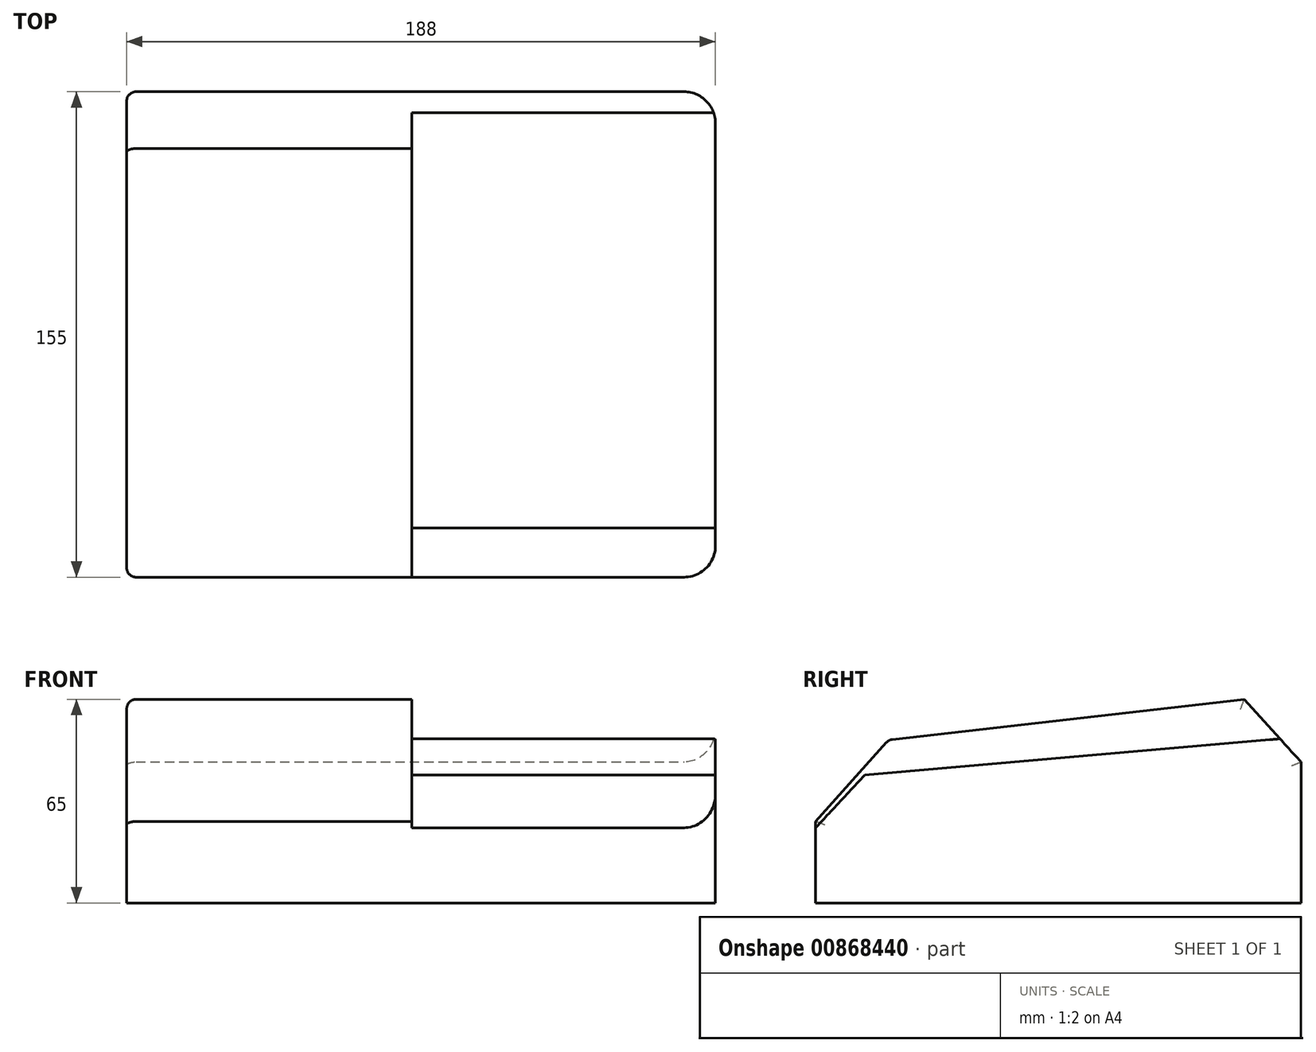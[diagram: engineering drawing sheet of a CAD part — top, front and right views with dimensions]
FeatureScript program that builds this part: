
annotation { "Feature Type Name" : "Feature", "Feature Type Description" : "" }
export const myFeature = defineFeature(function(context is Context, id is Id, definition is map)
    precondition{}
    {
        {
            var Q0;
            Q0=qCreatedBy(makeId("Top.planeOp"),FACE);
            var sketch = newSketch(context, id + "F0", { "sketchPlane" : qUnion([Q0])});
            skLineSegment(sketch, "E0.bottom", {"start": v(0, 155) * mm, "end": v(188, 155) * mm});
            skLineSegment(sketch, "E0.top", {"start": v(0, 0) * mm, "end": v(188, 0) * mm});
            skLineSegment(sketch, "E0.left", {"start": v(0, 155) * mm, "end": v(0, 0) * mm});
            skLineSegment(sketch, "E0.right", {"start": v(188, 155) * mm, "end": v(188, 0) * mm});
            skPoint(sketch, "E1", {"position": v(0, 77.5) * mm});
            skCircle(sketch, "E2", {"center": v(15, 141) * mm, "radius": 4 * mm});
            skCircle(sketch, "E3", {"center": v(175, 141) * mm, "radius": 4 * mm});
            skCircle(sketch, "E4", {"center": v(175, 15) * mm, "radius": 4 * mm});
            skCircle(sketch, "E5", {"center": v(15, 15) * mm, "radius": 4 * mm});
            skLineSegment(sketch, "E6", {"start": v(0, 150) * mm, "end": v(15, 150) * mm});
            skLineSegment(sketch, "E7", {"start": v(15, 132) * mm, "end": v(0, 132) * mm});
            skArc(sketch, "E8", {"start": v(15, 150) * mm, "mid": v(6, 141) * mm, "end": v(15, 132) * mm, "construction": true});
            skArc(sketch, "E9", {"start": v(15, 132) * mm, "mid": v(24, 141) * mm, "end": v(15, 150) * mm});
            skLineSegment(sketch, "E10", {"start": v(15, 24) * mm, "end": v(0, 24) * mm});
            skLineSegment(sketch, "E11", {"start": v(15, 6) * mm, "end": v(0, 6) * mm});
            skLineSegment(sketch, "E12", {"start": v(175, 24) * mm, "end": v(188, 24) * mm});
            skLineSegment(sketch, "E13", {"start": v(175, 6) * mm, "end": v(188, 6) * mm});
            skLineSegment(sketch, "E14", {"start": v(175, 150) * mm, "end": v(188, 150) * mm});
            skLineSegment(sketch, "E15", {"start": v(175, 132) * mm, "end": v(188, 132) * mm});
            skArc(sketch, "E16", {"start": v(175, 150) * mm, "mid": v(166, 141) * mm, "end": v(175, 132) * mm});
            skArc(sketch, "E17", {"start": v(175, 132) * mm, "mid": v(184, 141) * mm, "end": v(175, 150) * mm, "construction": true});
            skArc(sketch, "E18", {"start": v(175, 24) * mm, "mid": v(166, 15) * mm, "end": v(175, 6) * mm});
            skArc(sketch, "E19", {"start": v(175, 6) * mm, "mid": v(184, 15) * mm, "end": v(175, 24) * mm, "construction": true});
            skArc(sketch, "E20", {"start": v(15, 6) * mm, "mid": v(24, 15) * mm, "end": v(15, 24) * mm});
            skArc(sketch, "E21", {"start": v(15, 24) * mm, "mid": v(6, 15) * mm, "end": v(15, 6) * mm, "construction": true});
            skLineSegment(sketch, "E22.0", {"start": v(3, 3) * mm, "end": v(185, 3) * mm});
            skLineSegment(sketch, "E22.1", {"start": v(3, 152) * mm, "end": v(3, 3) * mm});
            skLineSegment(sketch, "E22.2", {"start": v(3, 152) * mm, "end": v(185, 152) * mm});
            skLineSegment(sketch, "E22.3", {"start": v(185, 152) * mm, "end": v(185, 3) * mm});
            skSolve(sketch);
        }
        {
            var Q0;
            {var subQ11=sQuery(id+"F0.wireOp",EDGE,"E9");Q0=makeQuery(id+"F0.imprint","IMPRINT",FACE,{"disambiguationData":[TD([[makeQuery(id+"F0.imprint","IMPRINT",EDGE,{"derivedFrom":subQ11}),-1.0]])]});}
            var Q1;
            {var subQ6=sQuery(id+"F0.wireOp",EDGE,"E0.bottom");Q1=makeQuery(id+"F0.imprint","IMPRINT",FACE,{"disambiguationData":[TD([[makeQuery(id+"F0.imprint","IMPRINT",EDGE,{"derivedFrom":subQ6}),-1.0]])]});}
            var Q2;
            Q2=makeQuery(id+"F0.imprint","IMPRINT",FACE,{"disambiguationData":[TD([[makeQuery(id+"F0.imprint","IMPRINT",EDGE,{"derivedFrom":sQuery(id+"F0.wireOp",EDGE,"E2")}),-1.0]])]});
            var Q3;
            {var subQ0=sQuery(id+"F0.wireOp",EDGE,"E6");var subQ1=sQuery(id+"F0.wireOp",EDGE,"E0.left");var subQ2=makeQuery(id+"F0.imprint","INTERSECT",VERTEX,{"derivedFrom":[subQ1,subQ0]});Q3=makeQuery(id+"F0.imprint","IMPRINT",FACE,{"disambiguationData":[TD([[makeQuery(id+"F0.imprint","IMPRINT",EDGE,{"disambiguationData":[TD([[subQ2,-1.0]])],"derivedFrom":subQ1}),1.0]])]});}
            var Q4;
            Q4=makeQuery(id+"F0.imprint","IMPRINT",FACE,{"disambiguationData":[TD([[makeQuery(id+"F0.imprint","IMPRINT",EDGE,{"derivedFrom":sQuery(id+"F0.wireOp",EDGE,"E2")}),1.0]])]});
            var Q5;
            {var subQ0=sQuery(id+"F0.wireOp",EDGE,"E7");var subQ1=sQuery(id+"F0.wireOp",EDGE,"E0.left");var subQ2=makeQuery(id+"F0.imprint","INTERSECT",VERTEX,{"derivedFrom":[subQ1,subQ0]});Q5=makeQuery(id+"F0.imprint","IMPRINT",FACE,{"disambiguationData":[TD([[makeQuery(id+"F0.imprint","IMPRINT",EDGE,{"disambiguationData":[TD([[subQ2,-1.0]])],"derivedFrom":subQ1}),1.0]])]});}
            var Q6;
            Q6=makeQuery(id+"F0.imprint","IMPRINT",FACE,{"disambiguationData":[TD([[makeQuery(id+"F0.imprint","IMPRINT",EDGE,{"derivedFrom":sQuery(id+"F0.wireOp",EDGE,"E5")}),-1.0]])]});
            var Q7;
            Q7=makeQuery(id+"F0.imprint","IMPRINT",FACE,{"disambiguationData":[TD([[makeQuery(id+"F0.imprint","IMPRINT",EDGE,{"derivedFrom":sQuery(id+"F0.wireOp",EDGE,"E5")}),1.0]])]});
            var Q8;
            {var subQ0=sQuery(id+"F0.wireOp",EDGE,"E10");var subQ1=sQuery(id+"F0.wireOp",EDGE,"E0.left");var subQ2=makeQuery(id+"F0.imprint","INTERSECT",VERTEX,{"derivedFrom":[subQ1,subQ0]});Q8=makeQuery(id+"F0.imprint","IMPRINT",FACE,{"disambiguationData":[TD([[makeQuery(id+"F0.imprint","IMPRINT",EDGE,{"disambiguationData":[TD([[subQ2,-1.0]])],"derivedFrom":subQ1}),1.0]])]});}
            var Q9;
            {var subQ6=sQuery(id+"F0.wireOp",EDGE,"E0.top");Q9=makeQuery(id+"F0.imprint","IMPRINT",FACE,{"disambiguationData":[TD([[makeQuery(id+"F0.imprint","IMPRINT",EDGE,{"derivedFrom":subQ6}),1.0]])]});}
            var Q10;
            Q10=makeQuery(id+"F0.imprint","IMPRINT",FACE,{"disambiguationData":[TD([[makeQuery(id+"F0.imprint","IMPRINT",EDGE,{"derivedFrom":sQuery(id+"F0.wireOp",EDGE,"E4")}),-1.0]])]});
            var Q11;
            Q11=makeQuery(id+"F0.imprint","IMPRINT",FACE,{"disambiguationData":[TD([[makeQuery(id+"F0.imprint","IMPRINT",EDGE,{"derivedFrom":sQuery(id+"F0.wireOp",EDGE,"E4")}),1.0]])]});
            var Q12;
            {var subQ0=sQuery(id+"F0.wireOp",EDGE,"E12");var subQ1=sQuery(id+"F0.wireOp",EDGE,"E0.right");var subQ2=makeQuery(id+"F0.imprint","INTERSECT",VERTEX,{"derivedFrom":[subQ1,subQ0]});Q12=makeQuery(id+"F0.imprint","IMPRINT",FACE,{"disambiguationData":[TD([[makeQuery(id+"F0.imprint","IMPRINT",EDGE,{"disambiguationData":[TD([[subQ2,-1.0]])],"derivedFrom":subQ1}),-1.0]])]});}
            var Q13;
            {var subQ0=sQuery(id+"F0.wireOp",EDGE,"E12");var subQ1=sQuery(id+"F0.wireOp",EDGE,"E0.right");var subQ2=makeQuery(id+"F0.imprint","INTERSECT",VERTEX,{"derivedFrom":[subQ1,subQ0]});Q13=makeQuery(id+"F0.imprint","IMPRINT",FACE,{"disambiguationData":[TD([[makeQuery(id+"F0.imprint","IMPRINT",EDGE,{"disambiguationData":[TD([[subQ2,1.0]])],"derivedFrom":subQ1}),-1.0]])]});}
            var Q14;
            {var subQ0=sQuery(id+"F0.wireOp",EDGE,"E14");var subQ1=sQuery(id+"F0.wireOp",EDGE,"E0.right");var subQ2=makeQuery(id+"F0.imprint","INTERSECT",VERTEX,{"derivedFrom":[subQ1,subQ0]});Q14=makeQuery(id+"F0.imprint","IMPRINT",FACE,{"disambiguationData":[TD([[makeQuery(id+"F0.imprint","IMPRINT",EDGE,{"disambiguationData":[TD([[subQ2,-1.0]])],"derivedFrom":subQ1}),-1.0]])]});}
            var Q15;
            Q15=makeQuery(id+"F0.imprint","IMPRINT",FACE,{"disambiguationData":[TD([[makeQuery(id+"F0.imprint","IMPRINT",EDGE,{"derivedFrom":sQuery(id+"F0.wireOp",EDGE,"E3")}),-1.0]])]});
            var Q16;
            Q16=makeQuery(id+"F0.imprint","IMPRINT",FACE,{"disambiguationData":[TD([[makeQuery(id+"F0.imprint","IMPRINT",EDGE,{"derivedFrom":sQuery(id+"F0.wireOp",EDGE,"E3")}),1.0]])]});
            extrude(context, id + "F1", {"entities" : qUnion([Q0, Q1, Q2, Q3, Q4, Q5, Q6, Q7, Q8, Q9, Q10, Q11, Q12, Q13, Q14, Q15, Q16]), "depth" : 65 * mm, "offsetDistance" : 25 * mm});
        }
        {
            var Q0;
            Q0=makeQuery(id+"F1.opExtrude","SWEPT_FACE",FACE,{"disambiguationData":[OSD([sQuery(id+"F0.wireOp",EDGE,"E0.right")])]});
            var sketch = newSketch(context, id + "F2", { "sketchPlane" : qUnion([Q0])});
            skLineSegment(sketch, "E23.0.0", {"start": v(0, 0) * mm, "end": v(155, 0) * mm});
            skLineSegment(sketch, "E23.0.1", {"start": v(155, 0) * mm, "end": v(155, 65) * mm});
            skLineSegment(sketch, "E23.0.2", {"start": v(155, 65) * mm, "end": v(0, 65) * mm});
            skLineSegment(sketch, "E23.0.3", {"start": v(0, 65) * mm, "end": v(0, 0) * mm});
            skLineSegment(sketch, "E24", {"start": v(0, 24) * mm, "end": v(15.69, 40.82) * mm});
            skLineSegment(sketch, "E25", {"start": v(15.69, 40.82) * mm, "end": v(148.28, 52.4) * mm});
            skLineSegment(sketch, "E26", {"start": v(155, 45) * mm, "end": v(136.86, 65) * mm});
            skLineSegment(sketch, "E27", {"start": v(136.86, 65) * mm, "end": v(23.36, 52.06) * mm});
            skLineSegment(sketch, "E28", {"start": v(23.36, 52.06) * mm, "end": v(0, 26) * mm});
            skSolve(sketch);
        }
        {
            var Q0;
            {var subQ3=sQuery(id+"F2.wireOp",EDGE,"E27");Q0=makeQuery(id+"F2.imprint","IMPRINT",FACE,{"disambiguationData":[TD([[makeQuery(id+"F2.imprint","IMPRINT",EDGE,{"derivedFrom":subQ3}),-1.0]])]});}
            var Q1;
            {var subQ0=sQuery(id+"F2.wireOp",EDGE,"E23.0.2");var subQ1=sQuery(id+"F2.wireOp",EDGE,"E23.0.1");var subQ2=makeQuery(id+"F2.imprint","INTERSECT",VERTEX,{"derivedFrom":[subQ1,subQ0]});Q1=makeQuery(id+"F2.imprint","IMPRINT",FACE,{"disambiguationData":[TD([[makeQuery(id+"F2.imprint","IMPRINT",EDGE,{"disambiguationData":[TD([[subQ2,-1.0]])],"derivedFrom":subQ1}),-1.0]])]});}
            extrude(context, id + "F3", {"entities" : qUnion([Q0, Q1]), "operationType" : NewBodyOperationType.REMOVE, "endBound" : BoundingType.THROUGH_ALL, "oppositeDirection" : true, "depth" : 25 * mm, "offsetDistance" : 25 * mm});
        }
        {
            var Q0;
            {var subQ1=sQuery(id+"F2.wireOp",EDGE,"E24");Q0=makeQuery(id+"F2.imprint","IMPRINT",FACE,{"disambiguationData":[TD([[makeQuery(id+"F2.imprint","IMPRINT",EDGE,{"derivedFrom":subQ1}),1.0]])]});}
            extrude(context, id + "F4", {"entities" : qUnion([Q0]), "operationType" : NewBodyOperationType.REMOVE, "oppositeDirection" : true, "depth" : 97 * mm, "offsetDistance" : 25 * mm});
        }
        {
            var Q0;
            Q0=makeQuery(id+"F3.boolean.opBoolean","COPY",EDGE,{"derivedFrom":makeQuery(id+"F3.opExtrude","SWEPT_EDGE",EDGE,{"disambiguationData":[OSD([sQuery(id+"F2.wireOp",EDGE,"E23.0.3"),sQuery(id+"F2.wireOp",EDGE,"E28")])]})});
            var Q1;
            Q1=makeQuery(id+"F3.boolean.opBoolean","COPY",EDGE,{"derivedFrom":makeQuery(id+"F3.opExtrude","SWEPT_EDGE",EDGE,{"disambiguationData":[OSD([sQuery(id+"F2.wireOp",EDGE,"E27"),sQuery(id+"F2.wireOp",EDGE,"E28")])]})});
            var Q2;
            Q2=makeQuery(id+"F3.boolean.opBoolean","INTERSECT",EDGE,{"derivedFrom":[makeQuery(id+"F1.opExtrude","SWEPT_FACE",FACE,{"disambiguationData":[OSD([sQuery(id+"F0.wireOp",EDGE,"E0.left")])]}),makeQuery(id+"F3.opExtrude","SWEPT_FACE",FACE,{"disambiguationData":[OSD([sQuery(id+"F2.wireOp",EDGE,"E27")])]})]});
            var Q3;
            Q3=makeQuery(id+"F3.boolean.opBoolean","INTERSECT",EDGE,{"derivedFrom":[makeQuery(id+"F1.opExtrude","SWEPT_FACE",FACE,{"disambiguationData":[OSD([sQuery(id+"F0.wireOp",EDGE,"E0.left")])]}),makeQuery(id+"F3.opExtrude","SWEPT_FACE",FACE,{"disambiguationData":[OSD([sQuery(id+"F2.wireOp",EDGE,"E28")])]})]});
            var Q4;
            Q4=makeQuery(id+"F1.opExtrude","SWEPT_EDGE",EDGE,{"disambiguationData":[OSD([sQuery(id+"F0.wireOp",EDGE,"E0.top"),sQuery(id+"F0.wireOp",EDGE,"E0.left")])]});
            var Q5;
            Q5=makeQuery(id+"F4.boolean.opBoolean","COPY",EDGE,{"derivedFrom":makeQuery(id+"F4.opExtrude","CAP_EDGE",EDGE,{"disambiguationData":[OSD([sQuery(id+"F2.wireOp",EDGE,"E27")])],"isStart":false})});
            var Q6;
            Q6=makeQuery(id+"F4.boolean.opBoolean","COPY",EDGE,{"derivedFrom":makeQuery(id+"F4.opExtrude","CAP_EDGE",EDGE,{"disambiguationData":[OSD([sQuery(id+"F2.wireOp",EDGE,"E28")])],"isStart":false})});
            var Q7;
            Q7=makeQuery(id+"F4.boolean.opBoolean","COPY",EDGE,{"derivedFrom":makeQuery(id+"F4.opExtrude","CAP_EDGE",EDGE,{"disambiguationData":[OSD([sQuery(id+"F2.wireOp",EDGE,"E26")])],"isStart":false})});
            var Q8;
            Q8=makeQuery(id+"F3.boolean.opBoolean","INTERSECT",EDGE,{"derivedFrom":[makeQuery(id+"F1.opExtrude","SWEPT_FACE",FACE,{"disambiguationData":[OSD([sQuery(id+"F0.wireOp",EDGE,"E0.left")])]}),makeQuery(id+"F3.opExtrude","SWEPT_FACE",FACE,{"disambiguationData":[OSD([sQuery(id+"F2.wireOp",EDGE,"E26")])]})]});
            var Q9;
            Q9=makeQuery(id+"F1.opExtrude","SWEPT_EDGE",EDGE,{"disambiguationData":[OSD([sQuery(id+"F0.wireOp",EDGE,"E0.bottom"),sQuery(id+"F0.wireOp",EDGE,"E0.left")])]});
            fillet(context, id + "F5", {"entities" : qUnion([Q0, Q1, Q2, Q3, Q4, Q5, Q6, Q7, Q8, Q9]), "radius" : 3 * mm, "tangentPropagation" : true, "allowEdgeOverflow" : false});
        }
        {
            var Q0;
            Q0=makeQuery(id+"F4.boolean.opBoolean","COPY",EDGE,{"derivedFrom":makeQuery(id+"F4.opExtrude","CAP_EDGE",EDGE,{"disambiguationData":[OSD([sQuery(id+"F2.wireOp",EDGE,"E25")])],"isStart":true})});
            var Q1;
            Q1=makeQuery(id+"F4.boolean.opBoolean","COPY",EDGE,{"derivedFrom":makeQuery(id+"F4.opExtrude","CAP_EDGE",EDGE,{"disambiguationData":[OSD([sQuery(id+"F2.wireOp",EDGE,"E24")])],"isStart":true})});
            var Q2;
            Q2=makeQuery(id+"F4.boolean.opBoolean","COPY",EDGE,{"derivedFrom":makeQuery(id+"F4.opExtrude","SWEPT_EDGE",EDGE,{"disambiguationData":[OSD([sQuery(id+"F2.wireOp",EDGE,"E23.0.3"),sQuery(id+"F2.wireOp",EDGE,"E24")])]})});
            var Q3;
            Q3=makeQuery(id+"F4.boolean.opBoolean","COPY",EDGE,{"derivedFrom":makeQuery(id+"F4.opExtrude","SWEPT_EDGE",EDGE,{"disambiguationData":[OSD([sQuery(id+"F2.wireOp",EDGE,"E25"),sQuery(id+"F2.wireOp",EDGE,"E26")])]})});
            var Q4;
            Q4=makeQuery(id+"F1.opExtrude","SWEPT_EDGE",EDGE,{"disambiguationData":[OSD([sQuery(id+"F0.wireOp",EDGE,"E0.top"),sQuery(id+"F0.wireOp",EDGE,"E0.right")])]});
            var Q5;
            Q5=makeQuery(id+"F1.opExtrude","SWEPT_EDGE",EDGE,{"disambiguationData":[OSD([sQuery(id+"F0.wireOp",EDGE,"E0.bottom"),sQuery(id+"F0.wireOp",EDGE,"E0.right")])]});
            fillet(context, id + "F6", {"entities" : qUnion([Q0, Q1, Q2, Q3, Q4, Q5]), "radius" : 10 * mm, "tangentPropagation" : true, "allowEdgeOverflow" : false});
        }
    });
